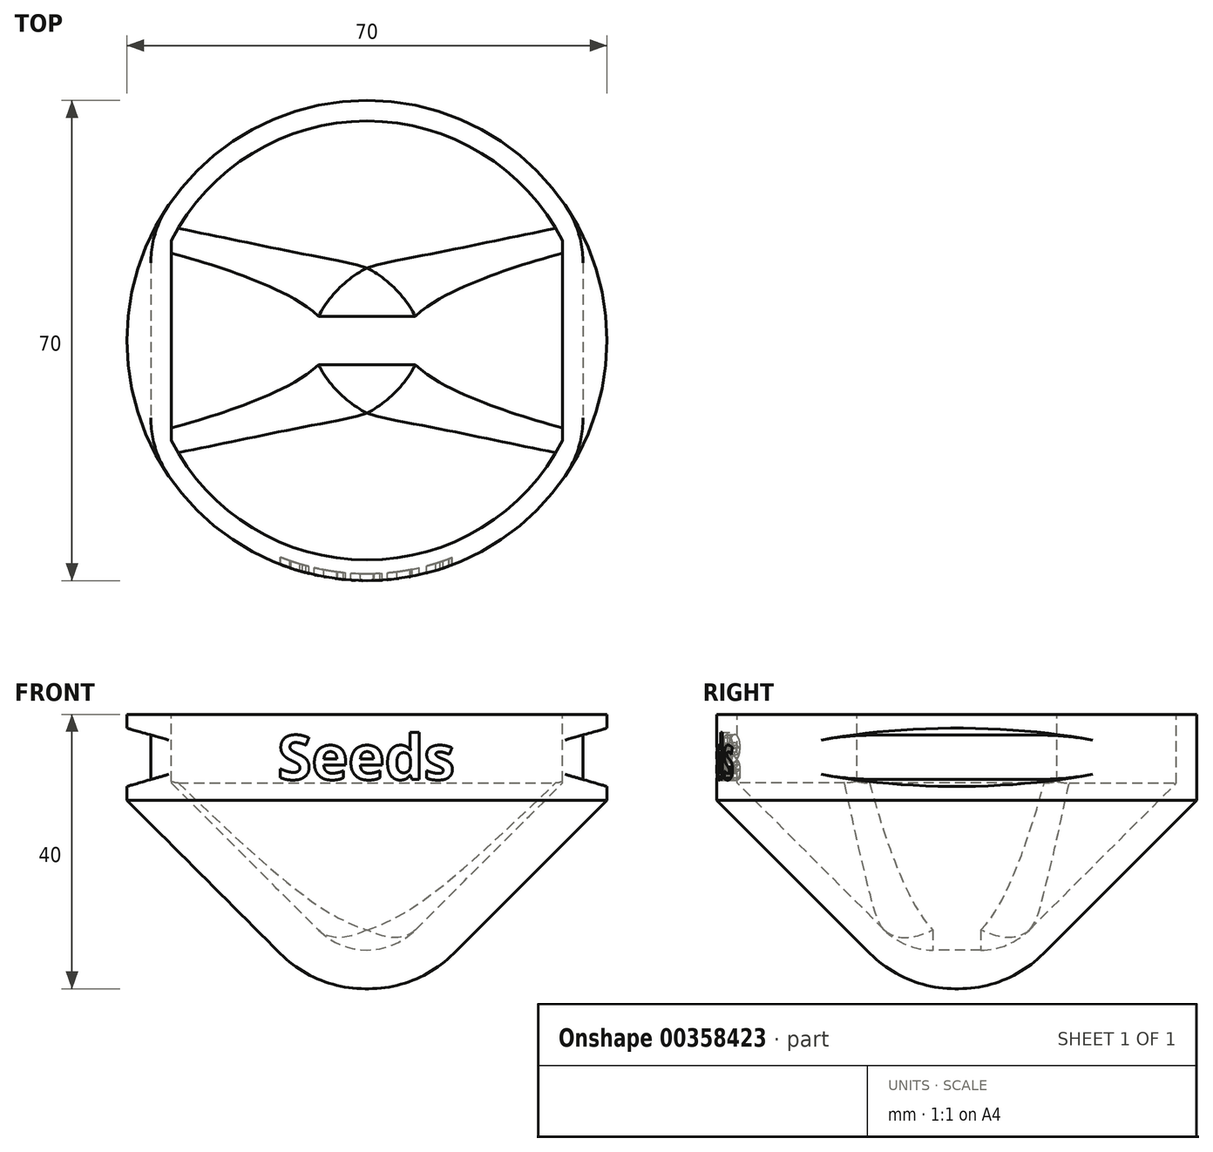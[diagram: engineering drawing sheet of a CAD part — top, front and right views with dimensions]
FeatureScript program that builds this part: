
annotation { "Feature Type Name" : "Feature", "Feature Type Description" : "" }
export const myFeature = defineFeature(function(context is Context, id is Id, definition is map)
    precondition{}
    {
        {
            var Q0;
            Q0=qCreatedBy(makeId("Top.planeOp"),FACE);
            var sketch = newSketch(context, id + "F0", { "sketchPlane" : qUnion([Q0])});
            skCircle(sketch, "E0", {"center": v(0, 0) * mm, "radius": 35 * mm});
            skSolve(sketch);
        }
        {
            var Q0;
            Q0=qSketchRegion(id+"F0",true);
            extrude(context, id + "F1", {"entities" : qUnion([Q0]), "depth" : 12.5 * mm});
        }
        {
            var Q0;
            Q0=qCreatedBy(makeId("Front.planeOp"),FACE);
            var sketch = newSketch(context, id + "F2", { "sketchPlane" : qUnion([Q0])});
            skText(sketch, "E1", { "text": "Seeds\n", "fontName": "OpenSans-Bold.ttf"});
            const initialGuessF2  = {"E1": [-0.01304, 0.003, 1, 0, 0.0065]};
            skSetInitialGuess(sketch, initialGuessF2);
            skSolve(sketch);
        }
        {
            var Q0;
            Q0=qSketchRegion(id+"F2",true);
            var Q1;
            Q1=makeQuery(id+"F1.opExtrude","SWEPT_FACE",FACE,{"disambiguationData":[OSD([sQuery(id+"F0.wireOp",EDGE,"E0")])]});
            extrude(context, id + "F3", {"entities" : qUnion([Q0]), "operationType" : NewBodyOperationType.REMOVE, "endBound" : BoundingType.THROUGH_ALL, "endBoundEntityFace" : qUnion([Q1]), "depth" : 25 * mm});
        }
        {
            var Q0;
            Q0=makeQuery(id+"F1.opExtrude","CAP_FACE",FACE,{"disambiguationData":[OSD([sQuery(id+"F0.wireOp",EDGE,"E0")])],"isStart":false});
            var sketch = newSketch(context, id + "F4", { "sketchPlane" : qUnion([Q0])});
            skCircle(sketch, "E2", {"center": v(0, 0) * mm, "radius": 34 * mm});
            skSolve(sketch);
        }
        {
            var Q0;
            Q0=qSketchRegion(id+"F4",true);
            var Q1;
            Q1=makeQuery(id+"F1.opExtrude","CAP_FACE",FACE,{"disambiguationData":[OSD([sQuery(id+"F0.wireOp",EDGE,"E0")])],"isStart":true});
            extrude(context, id + "F5", {"entities" : qUnion([Q0]), "operationType" : NewBodyOperationType.ADD, "endBound" : BoundingType.UP_TO_SURFACE, "oppositeDirection" : true, "endBoundEntityFace" : qUnion([Q1]), "depth" : 25 * mm});
        }
        {
            var Q0;
            Q0=qCreatedBy(makeId("Front.planeOp"),FACE);
            var sketch = newSketch(context, id + "F6", { "sketchPlane" : qUnion([Q0])});
            skLineSegment(sketch, "E3", {"start": v(-35, 10.5) * mm, "end": v(-35, 2) * mm});
            skLineSegment(sketch, "E4", {"start": v(-35, 2) * mm, "end": v(-31.5, 3) * mm});
            skLineSegment(sketch, "E5", {"start": v(-31.5, 3) * mm, "end": v(-31.5, 9.5) * mm});
            skLineSegment(sketch, "E6", {"start": v(-31.5, 9.5) * mm, "end": v(-35, 10.5) * mm});
            skLineSegment(sketch, "E7.MirrorCS", {"start": v(35, 10.5) * mm, "end": v(35, 2) * mm});
            skLineSegment(sketch, "E8.MirrorCS", {"start": v(31.5, 9.5) * mm, "end": v(35, 10.5) * mm});
            skLineSegment(sketch, "E9.MirrorCS", {"start": v(35, 2) * mm, "end": v(31.5, 3) * mm});
            skLineSegment(sketch, "E10.MirrorCS", {"start": v(31.5, 3) * mm, "end": v(31.5, 9.5) * mm});
            skSolve(sketch);
        }
        {
            var Q0;
            Q0=qSketchRegion(id+"F6",true);
            extrude(context, id + "F7", {"entities" : qUnion([Q0]), "operationType" : NewBodyOperationType.REMOVE, "endBound" : BoundingType.THROUGH_ALL, "oppositeDirection" : true, "depth" : 25 * mm, "hasSecondDirection" : true, "secondDirectionBound" : BoundingType.THROUGH_ALL, "secondDirectionOppositeDirection" : false, "secondDirectionDepth" : 25 * mm});
        }
        {
            var Q0;
            {var subQ0=sQuery(id+"F0.wireOp",EDGE,"E0");Q0=makeQuery(id+"F7.boolean.opBoolean","INTERSECT",EDGE,{"disambiguationData":[OD(0.0)],"derivedFrom":[makeQuery(id+"F3.boolean.opBoolean","SPLIT",FACE,{"disambiguationData":[TD([makeQuery(id+"F1.opExtrude","CAP_FACE",FACE,{"disambiguationData":[OSD([subQ0])],"isStart":true})])],"derivedFrom":makeQuery(id+"F1.opExtrude","SWEPT_FACE",FACE,{"disambiguationData":[OSD([subQ0])]})}),makeQuery(id+"F7.opExtrude","SWEPT_FACE",FACE,{"disambiguationData":[OSD([sQuery(id+"F6.wireOp",EDGE,"E5")])]})]});}
            var Q1;
            {var subQ0=sQuery(id+"F0.wireOp",EDGE,"E0");Q1=makeQuery(id+"F7.boolean.opBoolean","INTERSECT",EDGE,{"disambiguationData":[OD(0.0)],"derivedFrom":[makeQuery(id+"F3.boolean.opBoolean","SPLIT",FACE,{"disambiguationData":[TD([makeQuery(id+"F1.opExtrude","CAP_FACE",FACE,{"disambiguationData":[OSD([subQ0])],"isStart":true})])],"derivedFrom":makeQuery(id+"F1.opExtrude","SWEPT_FACE",FACE,{"disambiguationData":[OSD([subQ0])]})}),makeQuery(id+"F7.opExtrude","SWEPT_FACE",FACE,{"disambiguationData":[OSD([sQuery(id+"F6.wireOp",EDGE,"E10.MirrorCS")])]})]});}
            var Q2;
            {var subQ0=sQuery(id+"F0.wireOp",EDGE,"E0");Q2=makeQuery(id+"F7.boolean.opBoolean","INTERSECT",EDGE,{"disambiguationData":[OD(1.0)],"derivedFrom":[makeQuery(id+"F3.boolean.opBoolean","SPLIT",FACE,{"disambiguationData":[TD([makeQuery(id+"F1.opExtrude","CAP_FACE",FACE,{"disambiguationData":[OSD([subQ0])],"isStart":true})])],"derivedFrom":makeQuery(id+"F1.opExtrude","SWEPT_FACE",FACE,{"disambiguationData":[OSD([subQ0])]})}),makeQuery(id+"F7.opExtrude","SWEPT_FACE",FACE,{"disambiguationData":[OSD([sQuery(id+"F6.wireOp",EDGE,"E10.MirrorCS")])]})]});}
            var Q3;
            {var subQ0=sQuery(id+"F0.wireOp",EDGE,"E0");Q3=makeQuery(id+"F7.boolean.opBoolean","INTERSECT",EDGE,{"disambiguationData":[OD(1.0)],"derivedFrom":[makeQuery(id+"F3.boolean.opBoolean","SPLIT",FACE,{"disambiguationData":[TD([makeQuery(id+"F1.opExtrude","CAP_FACE",FACE,{"disambiguationData":[OSD([subQ0])],"isStart":true})])],"derivedFrom":makeQuery(id+"F1.opExtrude","SWEPT_FACE",FACE,{"disambiguationData":[OSD([subQ0])]})}),makeQuery(id+"F7.opExtrude","SWEPT_FACE",FACE,{"disambiguationData":[OSD([sQuery(id+"F6.wireOp",EDGE,"E5")])]})]});}
            fillet(context, id + "F8", {"entities" : qUnion([Q0, Q1, Q2, Q3]), "radius" : 15 * mm, "tangentPropagation" : true, "allowEdgeOverflow" : false});
        }
        {
            var Q0;
            Q0=makeQuery(id+"F1.opExtrude","CAP_FACE",FACE,{"disambiguationData":[OSD([sQuery(id+"F0.wireOp",EDGE,"E0")])],"isStart":true});
            var sketch = newSketch(context, id + "F9", { "sketchPlane" : qUnion([Q0])});
            skCircle(sketch, "E11.0.0", {"center": v(0, 0) * mm, "radius": 35 * mm});
            skSolve(sketch);
        }
        {
            var Q0;
            Q0=qSketchRegion(id+"F9",true);
            extrude(context, id + "F10", {"entities" : qUnion([Q0]), "operationType" : NewBodyOperationType.ADD, "depth" : 27.5 * mm, "hasDraft" : true, "draftAngle" : 45 * degree, "draftPullDirection" : true});
        }
        {
            var Q0;
            Q0=makeQuery(id+"F1.opExtrude","CAP_FACE",FACE,{"disambiguationData":[OSD([sQuery(id+"F0.wireOp",EDGE,"E0")])],"isStart":false});
            var sketch = newSketch(context, id + "F11", { "sketchPlane" : qUnion([Q0])});
            skArc(sketch, "E12", {"start": v(-28.5, -14.55) * mm, "mid": v(0, -32) * mm, "end": v(28.5, -14.55) * mm});
            skLineSegment(sketch, "E13", {"start": v(-28.5, 14.55) * mm, "end": v(-28.5, -14.55) * mm});
            skLineSegment(sketch, "E14", {"start": v(28.5, 14.55) * mm, "end": v(28.5, -14.55) * mm});
            skArc(sketch, "E15.trimOffspring", {"start": v(28.5, 14.55) * mm, "mid": v(0, 32) * mm, "end": v(-28.5, 14.55) * mm});
            skSolve(sketch);
        }
        {
            var Q0;
            Q0=qSketchRegion(id+"F11",true);
            extrude(context, id + "F12", {"entities" : qUnion([Q0]), "operationType" : NewBodyOperationType.REMOVE, "oppositeDirection" : true, "depth" : 10 * mm});
        }
        {
            var Q0;
            Q0=makeQuery(id+"F12.boolean.opBoolean","COPY",FACE,{"derivedFrom":makeQuery(id+"F12.opExtrude","CAP_FACE",FACE,{"disambiguationData":[OSD([sQuery(id+"F11.wireOp",EDGE,"E12"),sQuery(id+"F11.wireOp",EDGE,"E13"),sQuery(id+"F11.wireOp",EDGE,"E14"),sQuery(id+"F11.wireOp",EDGE,"E15.trimOffspring")])],"isStart":false})});
            var sketch = newSketch(context, id + "F13", { "sketchPlane" : qUnion([Q0])});
            skArc(sketch, "E16.0", {"start": v(28.5, 14.55) * mm, "mid": v(0, 32) * mm, "end": v(-28.5, 14.55) * mm});
            skLineSegment(sketch, "E17.0", {"start": v(-28.5, 14.55) * mm, "end": v(-28.5, -14.55) * mm});
            skArc(sketch, "E17.1", {"start": v(-28.5, -14.55) * mm, "mid": v(0, -32) * mm, "end": v(28.5, -14.55) * mm});
            skLineSegment(sketch, "E17.2", {"start": v(28.5, 14.55) * mm, "end": v(28.5, -14.55) * mm});
            skSolve(sketch);
        }
        {
            var Q0;
            Q0=qSketchRegion(id+"F13",true);
            extrude(context, id + "F14", {"entities" : qUnion([Q0]), "operationType" : NewBodyOperationType.REMOVE, "endBound" : BoundingType.THROUGH_ALL, "oppositeDirection" : true, "depth" : 45 * mm, "hasDraft" : true, "draftAngle" : 45 * degree, "draftPullDirection" : true});
        }
        {
            var Q0;
            Q0=makeQuery(id+"F14.boolean.opBoolean","COPY",EDGE,{"derivedFrom":makeQuery(id+"F14.*.draft.opDraft","SPLIT",EDGE,{"derivedFrom":makeQuery(id+"F14.opExtrude","SWEPT_EDGE",EDGE,{"disambiguationData":[OSD([sQuery(id+"F13.wireOp",EDGE,"E16.0"),sQuery(id+"F13.wireOp",EDGE,"E17.0")])]})})});
            var Q1;
            {var subQ0=sQuery(id+"F13.wireOp",EDGE,"E17.2");var subQ1=sQuery(id+"F13.wireOp",EDGE,"E16.0");var subQ2=sQuery(id+"F13.wireOp",EDGE,"E17.0");var subQ3=sQuery(id+"F13.wireOp",EDGE,"E17.1");Q1=makeQuery(id+"F14.boolean.opBoolean","COPY",EDGE,{"derivedFrom":makeQuery(id+"F14.*.draft.opDraft","MERGE",EDGE,{"derivedFrom":[makeQuery(id+"F14.opExtrude","SWEPT_EDGE",EDGE,{"disambiguationData":[OSD([subQ2,subQ3])]}),makeQuery(id+"F14.opExtrude","SWEPT_EDGE",EDGE,{"disambiguationData":[OSD([subQ3,subQ0])]}),makeQuery(id+"F14.opExtrude","SWEPT_EDGE",EDGE,{"disambiguationData":[OSD([subQ1,subQ2])]}),makeQuery(id+"F14.opExtrude","SWEPT_EDGE",EDGE,{"disambiguationData":[OSD([subQ1,subQ0])]})]})});}
            var Q2;
            Q2=makeQuery(id+"F14.boolean.opBoolean","COPY",EDGE,{"derivedFrom":makeQuery(id+"F14.*.draft.opDraft","SPLIT",EDGE,{"derivedFrom":makeQuery(id+"F14.opExtrude","SWEPT_EDGE",EDGE,{"disambiguationData":[OSD([sQuery(id+"F13.wireOp",EDGE,"E16.0"),sQuery(id+"F13.wireOp",EDGE,"E17.2")])]})})});
            var Q3;
            Q3=makeQuery(id+"F14.boolean.opBoolean","COPY",EDGE,{"derivedFrom":makeQuery(id+"F14.*.draft.opDraft","SPLIT",EDGE,{"derivedFrom":makeQuery(id+"F14.opExtrude","SWEPT_EDGE",EDGE,{"disambiguationData":[OSD([sQuery(id+"F13.wireOp",EDGE,"E17.1"),sQuery(id+"F13.wireOp",EDGE,"E17.2")])]})})});
            var Q4;
            Q4=makeQuery(id+"F14.boolean.opBoolean","COPY",EDGE,{"derivedFrom":makeQuery(id+"F14.*.draft.opDraft","SPLIT",EDGE,{"derivedFrom":makeQuery(id+"F14.opExtrude","SWEPT_EDGE",EDGE,{"disambiguationData":[OSD([sQuery(id+"F13.wireOp",EDGE,"E17.0"),sQuery(id+"F13.wireOp",EDGE,"E17.1")])]})})});
            fillet(context, id + "F15", {"entities" : qUnion([Q0, Q1, Q2, Q3, Q4]), "radius" : 10 * mm, "allowEdgeOverflow" : false});
        }
        {
            var Q0;
            Q0=makeQuery(id+"F10.opExtrude","CAP_EDGE",EDGE,{"disambiguationData":[OSD([sQuery(id+"F9.wireOp",EDGE,"E11.0.0")])],"isStart":false});
            fillet(context, id + "F16", {"entities" : qUnion([Q0]), "radius" : 17.5 * mm, "tangentPropagation" : true, "allowEdgeOverflow" : false});
        }
    });
